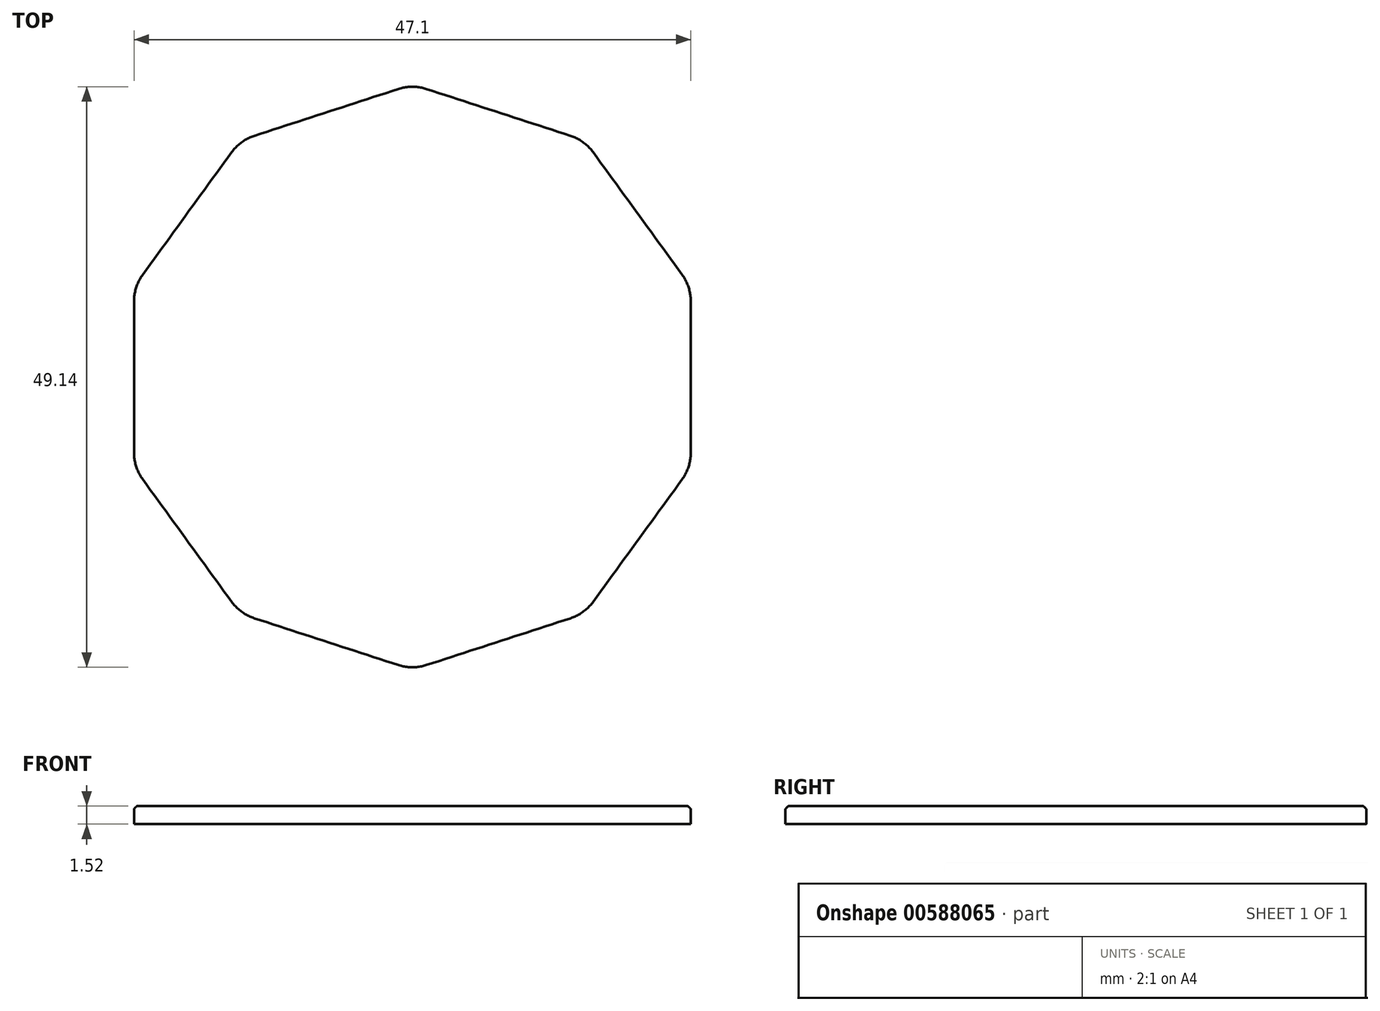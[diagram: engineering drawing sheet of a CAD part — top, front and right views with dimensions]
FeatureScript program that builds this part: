
annotation { "Feature Type Name" : "Feature", "Feature Type Description" : "" }
export const myFeature = defineFeature(function(context is Context, id is Id, definition is map)
    precondition{}
    {
        {
            var Q0;
            Q0=qCreatedBy(makeId("Top.planeOp"),FACE);
            var sketch = newSketch(context, id + "F0", { "sketchPlane" : qUnion([Q0])});
            skCircle(sketch, "E0.cCircle", {"center": v(0, 0) * mm, "radius": 26.09 * mm, "construction": true});
            skLineSegment(sketch, "E0.0", {"start": v(26.09, 8.48) * mm, "end": v(26.09, -8.48) * mm});
            skLineSegment(sketch, "E0.1", {"start": v(26.09, -8.48) * mm, "end": v(16.12, -22.2) * mm});
            skLineSegment(sketch, "E0.2", {"start": v(16.12, -22.2) * mm, "end": v(0, -27.43) * mm});
            skLineSegment(sketch, "E0.3", {"start": v(0, -27.43) * mm, "end": v(-16.12, -22.2) * mm});
            skLineSegment(sketch, "E0.4", {"start": v(-16.12, -22.2) * mm, "end": v(-26.09, -8.48) * mm});
            skLineSegment(sketch, "E0.5", {"start": v(-26.09, -8.48) * mm, "end": v(-26.09, 8.48) * mm});
            skLineSegment(sketch, "E0.6", {"start": v(-26.09, 8.48) * mm, "end": v(-16.12, 22.2) * mm});
            skLineSegment(sketch, "E0.7", {"start": v(-16.12, 22.2) * mm, "end": v(0, 27.43) * mm});
            skLineSegment(sketch, "E0.8", {"start": v(0, 27.43) * mm, "end": v(16.12, 22.2) * mm});
            skLineSegment(sketch, "E0.9", {"start": v(16.12, 22.2) * mm, "end": v(26.09, 8.48) * mm});
            skPoint(sketch, "E0.0.midPoint", {"position": v(26.09, 0) * mm});
            skSolve(sketch);
        }
        {
            var Q0;
            Q0=qSketchRegion(id+"F0",true);
            extrude(context, id + "F1", {"entities" : qUnion([Q0]), "endBound" : BoundingType.SYMMETRIC, "depth" : 10.16 * mm, "offsetDistance" : 25.4 * mm});
        }
        {
            var Q0;
            Q0=makeQuery(id+"F1.opExtrude","SWEPT_EDGE",EDGE,{"disambiguationData":[OSD([sQuery(id+"F0.wireOp",EDGE,"E0.3"),sQuery(id+"F0.wireOp",EDGE,"E0.4")])]});
            var Q1;
            Q1=makeQuery(id+"F1.opExtrude","SWEPT_EDGE",EDGE,{"disambiguationData":[OSD([sQuery(id+"F0.wireOp",EDGE,"E0.4"),sQuery(id+"F0.wireOp",EDGE,"E0.5")])]});
            var Q2;
            Q2=makeQuery(id+"F1.opExtrude","SWEPT_EDGE",EDGE,{"disambiguationData":[OSD([sQuery(id+"F0.wireOp",EDGE,"E0.5"),sQuery(id+"F0.wireOp",EDGE,"E0.6")])]});
            var Q3;
            Q3=makeQuery(id+"F1.opExtrude","SWEPT_EDGE",EDGE,{"disambiguationData":[OSD([sQuery(id+"F0.wireOp",EDGE,"E0.6"),sQuery(id+"F0.wireOp",EDGE,"E0.7")])]});
            var Q4;
            Q4=makeQuery(id+"F1.opExtrude","SWEPT_EDGE",EDGE,{"disambiguationData":[OSD([sQuery(id+"F0.wireOp",EDGE,"E0.7"),sQuery(id+"F0.wireOp",EDGE,"E0.8")])]});
            var Q5;
            Q5=makeQuery(id+"F1.opExtrude","SWEPT_EDGE",EDGE,{"disambiguationData":[OSD([sQuery(id+"F0.wireOp",EDGE,"E0.8"),sQuery(id+"F0.wireOp",EDGE,"E0.9")])]});
            var Q6;
            Q6=makeQuery(id+"F1.opExtrude","SWEPT_EDGE",EDGE,{"disambiguationData":[OSD([sQuery(id+"F0.wireOp",EDGE,"E0.0"),sQuery(id+"F0.wireOp",EDGE,"E0.9")])]});
            var Q7;
            Q7=makeQuery(id+"F1.opExtrude","SWEPT_EDGE",EDGE,{"disambiguationData":[OSD([sQuery(id+"F0.wireOp",EDGE,"E0.1"),sQuery(id+"F0.wireOp",EDGE,"E0.2")])]});
            var Q8;
            Q8=makeQuery(id+"F1.opExtrude","SWEPT_EDGE",EDGE,{"disambiguationData":[OSD([sQuery(id+"F0.wireOp",EDGE,"E0.2"),sQuery(id+"F0.wireOp",EDGE,"E0.3")])]});
            var Q9;
            Q9=makeQuery(id+"F1.opExtrude","SWEPT_EDGE",EDGE,{"disambiguationData":[OSD([sQuery(id+"F0.wireOp",EDGE,"E0.0"),sQuery(id+"F0.wireOp",EDGE,"E0.1")])]});
            fillet(context, id + "F2", {"entities" : qUnion([Q0, Q1, Q2, Q3, Q4, Q5, Q6, Q7, Q8, Q9]), "radius" : 6.35 * mm, "tangentPropagation" : true, "allowEdgeOverflow" : false});
        }
        {
            var Q0;
            Q0=makeQuery(id+"F1.opExtrude","CAP_FACE",FACE,{"disambiguationData":[OSD([sQuery(id+"F0.wireOp",EDGE,"E0.0"),sQuery(id+"F0.wireOp",EDGE,"E0.1"),sQuery(id+"F0.wireOp",EDGE,"E0.2"),sQuery(id+"F0.wireOp",EDGE,"E0.3"),sQuery(id+"F0.wireOp",EDGE,"E0.4"),sQuery(id+"F0.wireOp",EDGE,"E0.5"),sQuery(id+"F0.wireOp",EDGE,"E0.6"),sQuery(id+"F0.wireOp",EDGE,"E0.7"),sQuery(id+"F0.wireOp",EDGE,"E0.8"),sQuery(id+"F0.wireOp",EDGE,"E0.9")])],"isStart":true});
            fillet(context, id + "F3", {"entities" : qUnion([Q0]), "radius" : 1.27 * mm, "tangentPropagation" : true, "allowEdgeOverflow" : false});
        }
        {
            var Q0;
            Q0=makeQuery(id+"F1.opExtrude","CAP_FACE",FACE,{"disambiguationData":[OSD([sQuery(id+"F0.wireOp",EDGE,"E0.0"),sQuery(id+"F0.wireOp",EDGE,"E0.1"),sQuery(id+"F0.wireOp",EDGE,"E0.2"),sQuery(id+"F0.wireOp",EDGE,"E0.3"),sQuery(id+"F0.wireOp",EDGE,"E0.4"),sQuery(id+"F0.wireOp",EDGE,"E0.5"),sQuery(id+"F0.wireOp",EDGE,"E0.6"),sQuery(id+"F0.wireOp",EDGE,"E0.7"),sQuery(id+"F0.wireOp",EDGE,"E0.8"),sQuery(id+"F0.wireOp",EDGE,"E0.9")])],"isStart":false});
            var sketch = newSketch(context, id + "F4", { "sketchPlane" : qUnion([Q0])});
            skLineSegment(sketch, "E1.0", {"start": v(-22.82, -8.65) * mm, "end": v(-15.28, -19.03) * mm});
            skArc(sketch, "E1.1", {"start": v(-23.55, -6.41) * mm, "mid": v(-23.36, -7.6) * mm, "end": v(-22.82, -8.65) * mm});
            skLineSegment(sketch, "E1.2", {"start": v(-23.55, 6.41) * mm, "end": v(-23.55, -6.41) * mm});
            skArc(sketch, "E1.3", {"start": v(-22.82, 8.65) * mm, "mid": v(-23.36, 7.6) * mm, "end": v(-23.55, 6.41) * mm});
            skLineSegment(sketch, "E1.4", {"start": v(-15.28, 19.03) * mm, "end": v(-22.82, 8.65) * mm});
            skArc(sketch, "E1.5", {"start": v(-15.28, -19.03) * mm, "mid": v(-14.44, -19.87) * mm, "end": v(-13.38, -20.41) * mm});
            skArc(sketch, "E1.6", {"start": v(-13.38, 20.41) * mm, "mid": v(-14.44, 19.87) * mm, "end": v(-15.28, 19.03) * mm});
            skLineSegment(sketch, "E1.7", {"start": v(-1.18, 24.38) * mm, "end": v(-13.38, 20.41) * mm});
            skArc(sketch, "E1.8", {"start": v(1.18, 24.38) * mm, "mid": v(0, 24.57) * mm, "end": v(-1.18, 24.38) * mm});
            skLineSegment(sketch, "E1.9", {"start": v(13.38, 20.41) * mm, "end": v(1.18, 24.38) * mm});
            skArc(sketch, "E1.10", {"start": v(13.38, -20.41) * mm, "mid": v(14.44, -19.87) * mm, "end": v(15.28, -19.03) * mm});
            skLineSegment(sketch, "E1.11", {"start": v(1.18, -24.38) * mm, "end": v(13.38, -20.41) * mm});
            skArc(sketch, "E1.12", {"start": v(-1.18, -24.38) * mm, "mid": v(0, -24.57) * mm, "end": v(1.18, -24.38) * mm});
            skLineSegment(sketch, "E1.13", {"start": v(-13.38, -20.41) * mm, "end": v(-1.18, -24.38) * mm});
            skLineSegment(sketch, "E1.14", {"start": v(15.28, -19.03) * mm, "end": v(22.82, -8.65) * mm});
            skArc(sketch, "E1.15", {"start": v(22.82, -8.65) * mm, "mid": v(23.36, -7.6) * mm, "end": v(23.55, -6.41) * mm});
            skLineSegment(sketch, "E1.16", {"start": v(23.55, -6.41) * mm, "end": v(23.55, 6.41) * mm});
            skArc(sketch, "E1.17", {"start": v(23.55, 6.41) * mm, "mid": v(23.36, 7.6) * mm, "end": v(22.82, 8.65) * mm});
            skLineSegment(sketch, "E1.18", {"start": v(22.82, 8.65) * mm, "end": v(15.28, 19.03) * mm});
            skArc(sketch, "E1.19", {"start": v(15.28, 19.03) * mm, "mid": v(14.44, 19.87) * mm, "end": v(13.38, 20.41) * mm});
            skSolve(sketch);
        }
        {
            var Q0;
            Q0=makeQuery(id+"F4.imprint","IMPRINT",FACE,{"disambiguationData":[TD([[makeQuery(id+"F4.imprint","IMPRINT",EDGE,{"derivedFrom":sQuery(id+"F4.wireOp",EDGE,"E1.0")}),1.0]])]});
            extrude(context, id + "F5", {"entities" : qUnion([Q0]), "operationType" : NewBodyOperationType.REMOVE, "oppositeDirection" : true, "depth" : 1.27 * mm, "offsetDistance" : 25.4 * mm});
        }
        {
            var Q0;
            Q0=makeQuery(id+"F1.opExtrude","SWEPT_FACE",FACE,{"disambiguationData":[OSD([sQuery(id+"F0.wireOp",EDGE,"E0.0")])]});
            var sketch = newSketch(context, id + "F6", { "sketchPlane" : qUnion([Q0])});
            skPoint(sketch, "E2", {"position": v(0, 0) * mm});
            skSolve(sketch);
        }
        {
            var Q0;
            Q0=sQuery(id+"F6.wireOp",VERTEX,"E2");
            var Q1;
            Q1=makeQuery(id+"F1.opExtrude","SWEPT_BODY",BODY,{"disambiguationData":[OSD([sQuery(id+"F0.wireOp",EDGE,"E0.0"),sQuery(id+"F0.wireOp",EDGE,"E0.1"),sQuery(id+"F0.wireOp",EDGE,"E0.2"),sQuery(id+"F0.wireOp",EDGE,"E0.3"),sQuery(id+"F0.wireOp",EDGE,"E0.4"),sQuery(id+"F0.wireOp",EDGE,"E0.5"),sQuery(id+"F0.wireOp",EDGE,"E0.6"),sQuery(id+"F0.wireOp",EDGE,"E0.7"),sQuery(id+"F0.wireOp",EDGE,"E0.8"),sQuery(id+"F0.wireOp",EDGE,"E0.9")])]});
            hole(context, id + "F7", {"style" : HoleStyle.C_BORE, "endStyle" : HoleEndStyle.BLIND, "holeDiameter" : 3.8 * mm, "cBoreDiameter" : 5.08 * mm, "cBoreDepth" : 1.27 * mm, "majorDiameter" : 6.35 * mm, "holeDepth" : 12.7 * mm, "isTappedThrough" : true, "tappedDepth" : 12.7 * mm, "tapClearance" : 3, "locations" : qUnion([Q0]), "scope" : qUnion([Q1])});
        }
        {
            var Q0;
            Q0=makeQuery(id+"F1.opExtrude","CAP_FACE",FACE,{"disambiguationData":[OSD([sQuery(id+"F0.wireOp",EDGE,"E0.0"),sQuery(id+"F0.wireOp",EDGE,"E0.1"),sQuery(id+"F0.wireOp",EDGE,"E0.2"),sQuery(id+"F0.wireOp",EDGE,"E0.3"),sQuery(id+"F0.wireOp",EDGE,"E0.4"),sQuery(id+"F0.wireOp",EDGE,"E0.5"),sQuery(id+"F0.wireOp",EDGE,"E0.6"),sQuery(id+"F0.wireOp",EDGE,"E0.7"),sQuery(id+"F0.wireOp",EDGE,"E0.8"),sQuery(id+"F0.wireOp",EDGE,"E0.9")])],"isStart":false});
            extrude(context, id + "F8", {"entities" : qUnion([Q0]), "operationType" : NewBodyOperationType.REMOVE, "oppositeDirection" : true, "depth" : 25.4 * mm, "offsetDistance" : 25.4 * mm});
        }
        {
            var Q0;
            Q0=makeQuery(id+"F5.boolean.opBoolean","COPY",FACE,{"derivedFrom":makeQuery(id+"F5.opExtrude","CAP_FACE",FACE,{"disambiguationData":[OSD([sQuery(id+"F4.wireOp",EDGE,"E1.0"),sQuery(id+"F4.wireOp",EDGE,"E1.1"),sQuery(id+"F4.wireOp",EDGE,"E1.2"),sQuery(id+"F4.wireOp",EDGE,"E1.3"),sQuery(id+"F4.wireOp",EDGE,"E1.4"),sQuery(id+"F4.wireOp",EDGE,"E1.5"),sQuery(id+"F4.wireOp",EDGE,"E1.6"),sQuery(id+"F4.wireOp",EDGE,"E1.7"),sQuery(id+"F4.wireOp",EDGE,"E1.8"),sQuery(id+"F4.wireOp",EDGE,"E1.9"),sQuery(id+"F4.wireOp",EDGE,"E1.10"),sQuery(id+"F4.wireOp",EDGE,"E1.11"),sQuery(id+"F4.wireOp",EDGE,"E1.12"),sQuery(id+"F4.wireOp",EDGE,"E1.13"),sQuery(id+"F4.wireOp",EDGE,"E1.14"),sQuery(id+"F4.wireOp",EDGE,"E1.15"),sQuery(id+"F4.wireOp",EDGE,"E1.16"),sQuery(id+"F4.wireOp",EDGE,"E1.17"),sQuery(id+"F4.wireOp",EDGE,"E1.18"),sQuery(id+"F4.wireOp",EDGE,"E1.19")])],"isStart":false})});
            extrude(context, id + "F9", {"entities" : qUnion([Q0]), "operationType" : NewBodyOperationType.REMOVE, "oppositeDirection" : true, "depth" : 6.35 * mm, "offsetDistance" : 25.4 * mm});
        }
        {
            var Q0;
            Q0=makeQuery(id+"F9.boolean.opBoolean","COPY",FACE,{"derivedFrom":makeQuery(id+"F9.opExtrude","CAP_FACE",FACE,{"disambiguationData":[OSD([sQuery(id+"F4.wireOp",EDGE,"E1.0"),sQuery(id+"F4.wireOp",EDGE,"E1.1"),sQuery(id+"F4.wireOp",EDGE,"E1.2"),sQuery(id+"F4.wireOp",EDGE,"E1.3"),sQuery(id+"F4.wireOp",EDGE,"E1.4"),sQuery(id+"F4.wireOp",EDGE,"E1.5"),sQuery(id+"F4.wireOp",EDGE,"E1.6"),sQuery(id+"F4.wireOp",EDGE,"E1.7"),sQuery(id+"F4.wireOp",EDGE,"E1.8"),sQuery(id+"F4.wireOp",EDGE,"E1.9"),sQuery(id+"F4.wireOp",EDGE,"E1.10"),sQuery(id+"F4.wireOp",EDGE,"E1.11"),sQuery(id+"F4.wireOp",EDGE,"E1.12"),sQuery(id+"F4.wireOp",EDGE,"E1.13"),sQuery(id+"F4.wireOp",EDGE,"E1.14"),sQuery(id+"F4.wireOp",EDGE,"E1.15"),sQuery(id+"F4.wireOp",EDGE,"E1.16"),sQuery(id+"F4.wireOp",EDGE,"E1.17"),sQuery(id+"F4.wireOp",EDGE,"E1.18"),sQuery(id+"F4.wireOp",EDGE,"E1.19")])],"isStart":false})});
            extrude(context, id + "F10", {"entities" : qUnion([Q0]), "operationType" : NewBodyOperationType.REMOVE, "oppositeDirection" : true, "depth" : 1.02 * mm, "offsetDistance" : 25.4 * mm});
        }
        {
            var Q0;
            Q0=makeQuery(id+"F10.boolean.opBoolean","COPY",FACE,{"derivedFrom":makeQuery(id+"F10.opExtrude","CAP_FACE",FACE,{"disambiguationData":[OSD([sQuery(id+"F4.wireOp",EDGE,"E1.0"),sQuery(id+"F4.wireOp",EDGE,"E1.1"),sQuery(id+"F4.wireOp",EDGE,"E1.2"),sQuery(id+"F4.wireOp",EDGE,"E1.3"),sQuery(id+"F4.wireOp",EDGE,"E1.4"),sQuery(id+"F4.wireOp",EDGE,"E1.5"),sQuery(id+"F4.wireOp",EDGE,"E1.6"),sQuery(id+"F4.wireOp",EDGE,"E1.7"),sQuery(id+"F4.wireOp",EDGE,"E1.8"),sQuery(id+"F4.wireOp",EDGE,"E1.9"),sQuery(id+"F4.wireOp",EDGE,"E1.10"),sQuery(id+"F4.wireOp",EDGE,"E1.11"),sQuery(id+"F4.wireOp",EDGE,"E1.12"),sQuery(id+"F4.wireOp",EDGE,"E1.13"),sQuery(id+"F4.wireOp",EDGE,"E1.14"),sQuery(id+"F4.wireOp",EDGE,"E1.15"),sQuery(id+"F4.wireOp",EDGE,"E1.16"),sQuery(id+"F4.wireOp",EDGE,"E1.17"),sQuery(id+"F4.wireOp",EDGE,"E1.18"),sQuery(id+"F4.wireOp",EDGE,"E1.19")])],"isStart":false})});
            fillet(context, id + "F11", {"entities" : qUnion([Q0]), "radius" : 0.25 * mm, "tangentPropagation" : true, "rho" : .1, "crossSection" : FilletCrossSection.CONIC, "allowEdgeOverflow" : false});
        }
    });
